# Revit family: NLRS_57_AIR_UN_ceiling diffuser rrsv_LT_sacs
name_source: partatom
category: Air Terminals
units: mm (PartAtom-declared; Revit-internal decimal feet)

## family parameters
Always vertical = No
Cut with Voids When Loaded = No
OmniClass Number = 23.75.70.21.27.11
OmniClass Title = Diffusers, Registers, and Grilles
Part Type = Normal
Room Calculation Point = Yes
Round Connector Dimension = Use Diameter
Shared = No
Work Plane-Based = No

## types (5) — shared parameters
Assembly Code = 57.00
Description = Return grill with valve for use in ceiling or wall, Type RRSVMO and RRSVKO
FireRating = 00
IfcDescription = Return grill with valve for use in ceiling or wall, Type RRSVMO and RRSVKO
IfcExportAs = IfcAirTerminal
IfcExportType = Diffuser
IsExternal = No
LoadBearing = No
Manufacturer = Solid Air Climate Solutions
Model = RRSVMO/RRSVKO
NLRS_C_content_datum_uitgifte = 28-03-2022
NLRS_C_content_provider = Solid Air Climate Solutions
NLRS_C_content_versie = 3.19.02
NLRS_C_description = Return grill with valve for use in ceiling or wall, Type RRSVMO and RRSVKO
SACS_Article_Data = RRSV_Data
SACS_Factors = RRSV_Factors
SACS_Revised_by = J. Feeke
SACS_Revision_Date = 28-03-2022
SACS_Revision_Number = 3.19.02
URL = https://solid-air.nl

## per-type parameters (varying)
| type | Max Flow | Min Flow | NLRS_M_c01_diameter | SACS_Base_Index | SACS_Diameter | SACS_Diameter2 | SACS_Logo_Y | SACS_Radius_1 | SACS_Radius_2 | SACS_Radius_3 |
| 080 | 126.0 m³/h | 36.0 m³/h | 80 mm  [stored 0.262467 ft] | 1 | 80 mm  [stored 0.262467 ft] | 115 mm  [stored 0.377297 ft] | 47.5 mm | 39 mm  [stored 0.127953 ft] | 57.5 mm  [stored 0.188648 ft] | 10.25 mm |
| 200 | 360.0 m³/h | 180.0 m³/h | 200 mm  [stored 0.656168 ft] | 5 | 200 mm  [stored 0.656168 ft] | 248 mm  [stored 0.813648 ft] | 114 mm  [stored 0.374016 ft] | 99 mm | 124 mm  [stored 0.406824 ft] | 13.5 mm |
| 100 | 126.0 m³/h | 54.0 m³/h | 100 mm  [stored 0.328084 ft] | 2 | 100 mm  [stored 0.328084 ft] | 137 mm  [stored 0.449475 ft] | 58.5 mm  [stored 0.191929 ft] | 49 mm  [stored 0.160761 ft] | 68.5 mm  [stored 0.224738 ft] | 10.75 mm  [stored 0.035269 ft] |
| 125 | 144.0 m³/h | 72.0 m³/h | 125 mm  [stored 0.410105 ft] | 3 | 125 mm  [stored 0.410105 ft] | 161 mm  [stored 0.528215 ft] | 70.5 mm | 61.5 mm  [stored 0.201772 ft] | 80.5 mm  [stored 0.264108 ft] | 10.5 mm  [stored 0.0344488 ft] |
| 160 | 216.0 m³/h | 108.0 m³/h | 160 mm  [stored 0.524934 ft] | 4 | 160 mm  [stored 0.524934 ft] | 212 mm  [stored 0.695538 ft] | 96 mm  [stored 0.314961 ft] | 79 mm | 106 mm  [stored 0.347769 ft] | 14.5 mm |

note: [stored X ft] marks values corroborated as IEEE doubles in the binary element streams (Revit-internal decimal feet)

## geometry (parser evidence)
native form markers: Sweep x9
no freeform markers — native parametric forms only
